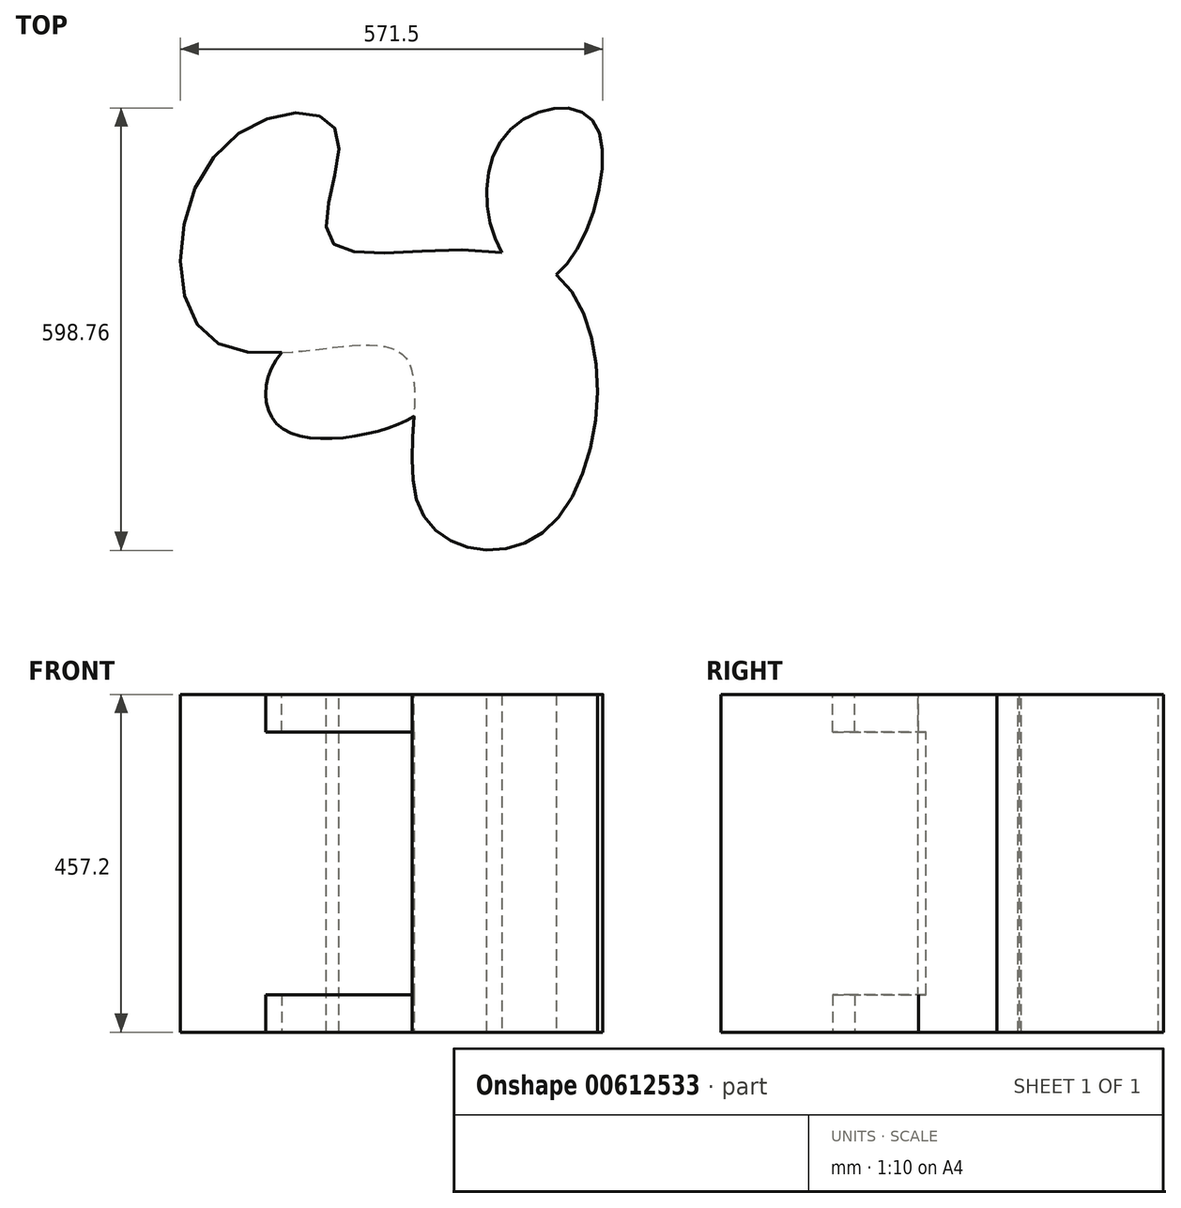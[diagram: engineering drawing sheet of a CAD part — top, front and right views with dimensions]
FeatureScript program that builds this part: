
annotation { "Feature Type Name" : "Feature", "Feature Type Description" : "" }
export const myFeature = defineFeature(function(context is Context, id is Id, definition is map)
    precondition{}
    {
        {
            var Q0;
            Q0=qCreatedBy(makeId("Top.planeOp"),FACE);
            var sketch = newSketch(context, id + "F0", { "sketchPlane" : qUnion([Q0])});
            skFitSpline(sketch, "E0", {"points": [v(-254.36, 218.28) * mm, v(-259.8, -42.41) * mm, v(-8.2, -57.86) * mm, v(17.24, -269.5) * mm, v(190.73, -293.12) * mm, v(193.45, 54.78) * mm, v(-103.57, 93.84) * mm, v(-97.21, 244.62) * mm, v(-254.36, 218.28) * mm]});
            skFitSpline(sketch, "E1", {"points": [v(127.23, 79.03) * mm, v(133.5, 240.08) * mm, v(252.5, 254.61) * mm, v(200.63, 49.21) * mm, v(127.23, 79.03) * mm]});
            skSolve(sketch);
        }
        {
            var Q0;
            Q0 = qSketchRegion(id + "F0", true);
            extrude(context, id + "F1", {"entities" : qUnion([Q0]), "depth" : 457.2 * mm, "offsetDistance" : 25.4 * mm});
        }
        {
            var Q0;
            Q0=qCreatedBy(makeId("Top.planeOp"),FACE);
            var sketch = newSketch(context, id + "F2", { "sketchPlane" : qUnion([Q0])});
            skFitSpline(sketch, "E2", {"points": [v(11.67, -140.46) * mm, v(-170.64, -158.57) * mm, v(-164.48, -50.32) * mm, v(0, -31) * mm, v(30.78, -94.63) * mm, v(11.67, -140.46) * mm]});
            skSolve(sketch);
        }
        {
            var Q0;
            Q0=makeQuery(id+"F2.imprint","IMPRINT",FACE,{"disambiguationData":[TD([[makeQuery(id+"F2.imprint","IMPRINT",EDGE,{"derivedFrom":sQuery(id+"F2.wireOp",EDGE,"E2")}),-1.0]])]});
            var Q1;
            Q1=makeQuery(id+"F1.opExtrude","CAP_FACE",FACE,{"disambiguationData":[OSD([sQuery(id+"F0.wireOp",EDGE,"E0"),sQuery(id+"F0.wireOp",EDGE,"E1")])],"isStart":false});
            extrude(context, id + "F3", {"entities" : qUnion([Q0, Q1]), "depth" : 50.8 * mm, "offsetDistance" : 25.4 * mm});
        }
        {
            var Q0;
            Q0=makeQuery(id+"F3.opExtrude","SWEPT_BODY",BODY,{"disambiguationData":[OSD([sQuery(id+"F0.wireOp",EDGE,"E0"),sQuery(id+"F0.wireOp",EDGE,"E1")])]});
            deleteBodies(context, id + "F4", {"entities" : qUnion([Q0])});
        }
        {
            var Q0;
            Q0=qCreatedBy(makeId("Top.planeOp"),FACE);
            cPlane(context, id + "F5", {"entities" : qUnion([Q0]), "cplaneType" : CPlaneType.OFFSET, "offset" : 228.6 * mm, "width" : 152.4 * mm, "height" : 152.4 * mm});
        }
        {
            var Q0;
            Q0=makeQuery(id+"F3.opExtrude","SWEPT_BODY",BODY,{"disambiguationData":[OSD([sQuery(id+"F2.wireOp",EDGE,"E2")])]});
            var Q1;
            Q1=qCreatedBy(id+"F5.planeOp",FACE);
            mirror(context, id + "F6", {"operationType" : NewBodyOperationType.ADD, "entities" : qUnion([Q0]), "mirrorPlane" : qUnion([Q1])});
        }
    });
